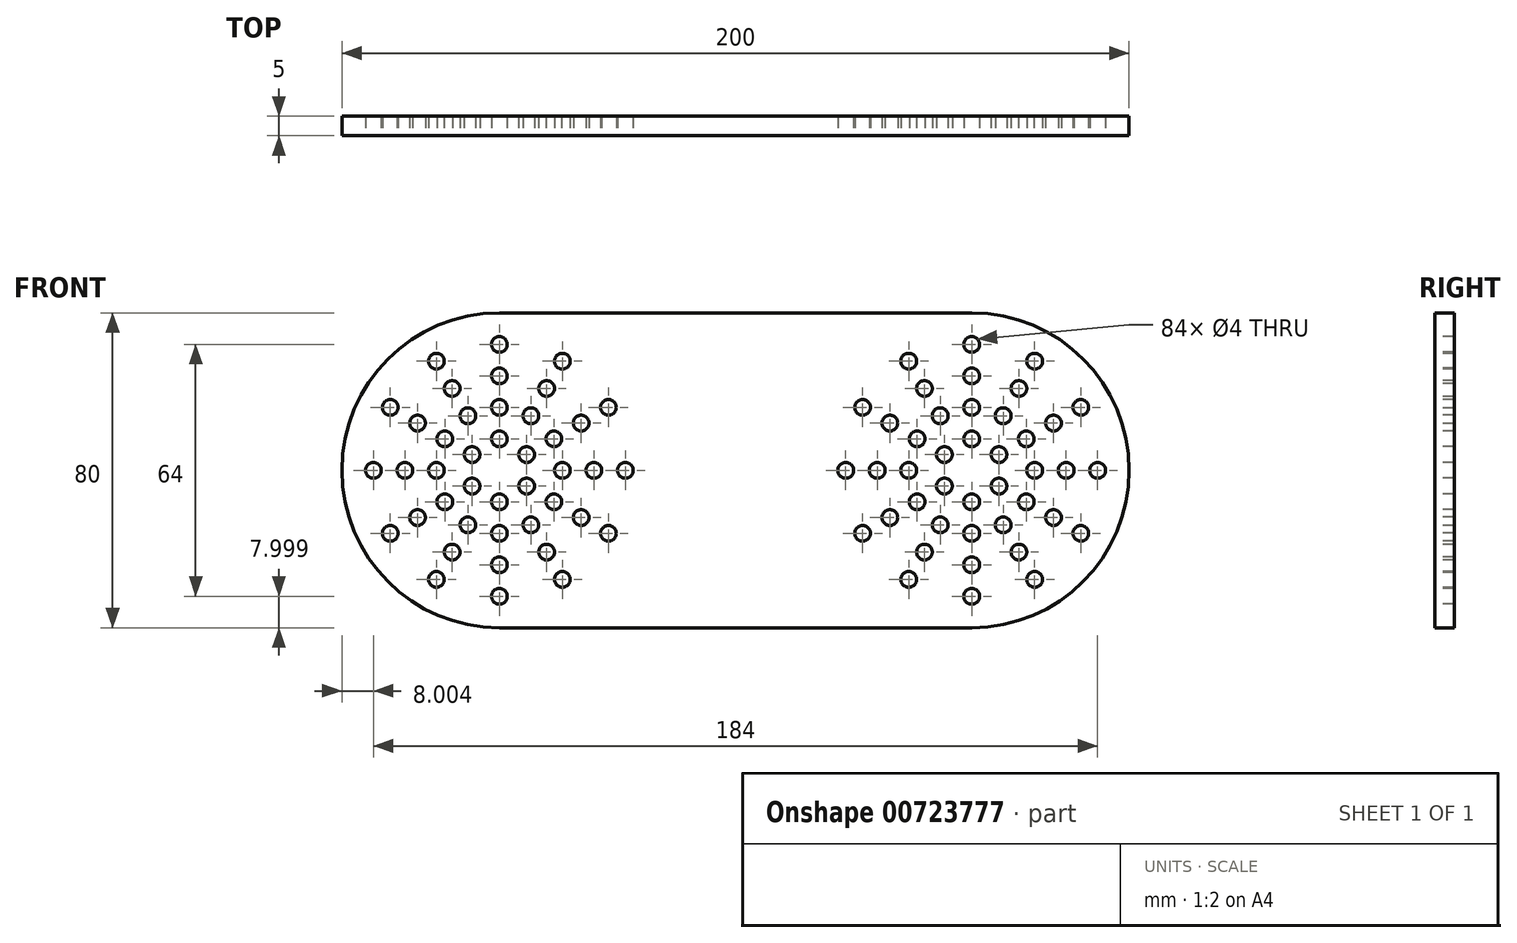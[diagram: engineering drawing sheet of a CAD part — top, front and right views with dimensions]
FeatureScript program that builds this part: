
annotation { "Feature Type Name" : "Feature", "Feature Type Description" : "" }
export const myFeature = defineFeature(function(context is Context, id is Id, definition is map)
    precondition{}
    {
        {
            var Q0;
            Q0=qCreatedBy(makeId("Front.planeOp"),FACE);
            var sketch = newSketch(context, id + "F0", { "sketchPlane" : qUnion([Q0])});
            skLineSegment(sketch, "E0.bottom", {"start": v(-63.67, 36.44) * mm, "end": v(56.33, 36.44) * mm});
            skLineSegment(sketch, "E0.top", {"start": v(-63.67, -43.56) * mm, "end": v(56.33, -43.56) * mm});
            skLineSegment(sketch, "E0.left", {"start": v(-103.67, -3.56) * mm, "end": v(-103.67, -3.56) * mm});
            skLineSegment(sketch, "E0.right", {"start": v(96.33, -3.56) * mm, "end": v(96.33, -3.56) * mm});
            skPoint(sketch, "E1.visualSharp", {"position": v(-103.67, 36.44) * mm});
            skArc(sketch, "E1.filletArc", {"start": v(-63.67, 36.44) * mm, "mid": v(-91.95, 24.72) * mm, "end": v(-103.67, -3.56) * mm});
            skPoint(sketch, "E2.visualSharp", {"position": v(-103.67, -43.56) * mm});
            skArc(sketch, "E2.filletArc", {"start": v(-103.67, -3.56) * mm, "mid": v(-91.95, -31.85) * mm, "end": v(-63.67, -43.56) * mm});
            skPoint(sketch, "E3.visualSharp", {"position": v(96.33, -43.56) * mm});
            skArc(sketch, "E3.filletArc", {"start": v(56.33, -43.56) * mm, "mid": v(84.62, -31.85) * mm, "end": v(96.33, -3.56) * mm});
            skPoint(sketch, "E4.visualSharp", {"position": v(96.33, 36.44) * mm});
            skArc(sketch, "E4.filletArc", {"start": v(96.33, -3.56) * mm, "mid": v(84.62, 24.72) * mm, "end": v(56.33, 36.44) * mm});
            skSolve(sketch);
        }
        {
            var Q0;
            Q0=makeQuery(id+"F0.imprint","IMPRINT",FACE,{"disambiguationData":[TD([[makeQuery(id+"F0.imprint","IMPRINT",EDGE,{"derivedFrom":sQuery(id+"F0.wireOp",EDGE,"E0.bottom")}),-1.0]])]});
            extrude(context, id + "F1", {"entities" : qUnion([Q0]), "depth" : 5 * mm});
        }
        {
            var Q0;
            Q0=makeQuery(id+"F1.opExtrude","CAP_FACE",FACE,{"disambiguationData":[OSD([sQuery(id+"F0.wireOp",EDGE,"E0.bottom"),sQuery(id+"F0.wireOp",EDGE,"E0.top"),sQuery(id+"F0.wireOp",EDGE,"E1.filletArc"),sQuery(id+"F0.wireOp",EDGE,"E2.filletArc"),sQuery(id+"F0.wireOp",EDGE,"E3.filletArc"),sQuery(id+"F0.wireOp",EDGE,"E4.filletArc")])],"isStart":false});
            var sketch = newSketch(context, id + "F2", { "sketchPlane" : qUnion([Q0])});
            skCircle(sketch, "E5", {"center": v(-63.67, -3.56) * mm, "radius": 33 * mm});
            skLineSegment(sketch, "E6", {"start": v(-3.67, 36.44) * mm, "end": v(-3.67, -43.56) * mm, "construction": true});
            skCircle(sketch, "E7.MirrorC", {"center": v(56.33, -3.56) * mm, "radius": 33 * mm});
            skSolve(sketch);
        }
        {
            var Q0;
            Q0=makeQuery(id+"F2.imprint","IMPRINT",FACE,{"disambiguationData":[TD([[makeQuery(id+"F2.imprint","IMPRINT",EDGE,{"derivedFrom":sQuery(id+"F2.wireOp",EDGE,"E5")}),1.0]])]});
            var sketch = newSketch(context, id + "F3", { "sketchPlane" : qUnion([Q0])});
            skCircle(sketch, "E8", {"center": v(-63.67, -3.56) * mm, "radius": 2 * mm, "construction": true});
            skCircle(sketch, "E9", {"center": v(-63.67, 28.44) * mm, "radius": 2 * mm});
            skCircle(sketch, "E10", {"center": v(-63.67, 20.44) * mm, "radius": 2 * mm});
            skCircle(sketch, "E11", {"center": v(-63.67, 12.44) * mm, "radius": 2 * mm});
            skCircle(sketch, "E12", {"center": v(-63.67, 4.44) * mm, "radius": 2 * mm});
            skCircle(sketch, "E13.1.0", {"center": v(-79.67, 24.15) * mm, "radius": 2 * mm});
            skCircle(sketch, "E13.1.1", {"center": v(-75.67, 17.22) * mm, "radius": 2 * mm});
            skCircle(sketch, "E13.1.2", {"center": v(-71.67, 10.3) * mm, "radius": 2 * mm});
            skCircle(sketch, "E13.2.0", {"center": v(-91.38, 12.44) * mm, "radius": 2 * mm});
            skCircle(sketch, "E13.2.1", {"center": v(-84.45, 8.44) * mm, "radius": 2 * mm});
            skCircle(sketch, "E13.2.2", {"center": v(-77.52, 4.44) * mm, "radius": 2 * mm});
            skCircle(sketch, "E13.2.3", {"center": v(-70.6, 0.44) * mm, "radius": 2 * mm});
            skCircle(sketch, "E13.3.0", {"center": v(-95.67, -3.56) * mm, "radius": 2 * mm});
            skCircle(sketch, "E13.3.1", {"center": v(-87.67, -3.56) * mm, "radius": 2 * mm});
            skCircle(sketch, "E13.3.2", {"center": v(-79.67, -3.56) * mm, "radius": 2 * mm});
            skCircle(sketch, "E13.4.0", {"center": v(-91.38, -19.56) * mm, "radius": 2 * mm});
            skCircle(sketch, "E13.4.1", {"center": v(-84.45, -15.56) * mm, "radius": 2 * mm});
            skCircle(sketch, "E13.4.2", {"center": v(-77.52, -11.56) * mm, "radius": 2 * mm});
            skCircle(sketch, "E13.4.3", {"center": v(-70.6, -7.56) * mm, "radius": 2 * mm});
            skCircle(sketch, "E13.5.0", {"center": v(-79.67, -31.27) * mm, "radius": 2 * mm});
            skCircle(sketch, "E13.5.1", {"center": v(-75.67, -24.35) * mm, "radius": 2 * mm});
            skCircle(sketch, "E13.5.2", {"center": v(-71.67, -17.42) * mm, "radius": 2 * mm});
            skCircle(sketch, "E13.6.0", {"center": v(-63.67, -35.56) * mm, "radius": 2 * mm});
            skCircle(sketch, "E13.6.1", {"center": v(-63.67, -27.56) * mm, "radius": 2 * mm});
            skCircle(sketch, "E13.6.2", {"center": v(-63.67, -19.56) * mm, "radius": 2 * mm});
            skCircle(sketch, "E13.6.3", {"center": v(-63.67, -11.56) * mm, "radius": 2 * mm});
            skCircle(sketch, "E13.7.0", {"center": v(-47.67, -31.27) * mm, "radius": 2 * mm});
            skCircle(sketch, "E13.7.1", {"center": v(-51.67, -24.35) * mm, "radius": 2 * mm});
            skCircle(sketch, "E13.7.2", {"center": v(-55.67, -17.42) * mm, "radius": 2 * mm});
            skCircle(sketch, "E13.8.0", {"center": v(-35.95, -19.56) * mm, "radius": 2 * mm});
            skCircle(sketch, "E13.8.1", {"center": v(-42.88, -15.56) * mm, "radius": 2 * mm});
            skCircle(sketch, "E13.8.2", {"center": v(-49.8, -11.56) * mm, "radius": 2 * mm});
            skCircle(sketch, "E13.8.3", {"center": v(-56.74, -7.56) * mm, "radius": 2 * mm});
            skCircle(sketch, "E13.9.0", {"center": v(-31.67, -3.56) * mm, "radius": 2 * mm});
            skCircle(sketch, "E13.9.1", {"center": v(-39.67, -3.56) * mm, "radius": 2 * mm});
            skCircle(sketch, "E13.9.2", {"center": v(-47.67, -3.56) * mm, "radius": 2 * mm});
            skCircle(sketch, "E13.10.0", {"center": v(-35.95, 12.44) * mm, "radius": 2 * mm});
            skCircle(sketch, "E13.10.1", {"center": v(-42.88, 8.44) * mm, "radius": 2 * mm});
            skCircle(sketch, "E13.10.2", {"center": v(-49.8, 4.44) * mm, "radius": 2 * mm});
            skCircle(sketch, "E13.10.3", {"center": v(-56.74, 0.44) * mm, "radius": 2 * mm});
            skCircle(sketch, "E13.11.0", {"center": v(-47.67, 24.15) * mm, "radius": 2 * mm});
            skCircle(sketch, "E13.11.1", {"center": v(-51.67, 17.22) * mm, "radius": 2 * mm});
            skCircle(sketch, "E13.11.2", {"center": v(-55.67, 10.3) * mm, "radius": 2 * mm});
            skCircle(sketch, "E14.MirrorC", {"center": v(56.33, -3.56) * mm, "radius": 2 * mm, "construction": true});
            skCircle(sketch, "E15.MirrorC", {"center": v(63.26, -7.56) * mm, "radius": 2 * mm});
            skCircle(sketch, "E16.MirrorC", {"center": v(49.4, -7.56) * mm, "radius": 2 * mm});
            skCircle(sketch, "E17.MirrorC", {"center": v(49.4, 0.44) * mm, "radius": 2 * mm});
            skCircle(sketch, "E18.MirrorC", {"center": v(56.33, 20.44) * mm, "radius": 2 * mm});
            skCircle(sketch, "E19.MirrorC", {"center": v(56.33, 4.44) * mm, "radius": 2 * mm});
            skCircle(sketch, "E20.MirrorC", {"center": v(77.12, -15.56) * mm, "radius": 2 * mm});
            skCircle(sketch, "E21.MirrorC", {"center": v(63.26, 0.44) * mm, "radius": 2 * mm});
            skCircle(sketch, "E22.MirrorC", {"center": v(56.33, -27.56) * mm, "radius": 2 * mm});
            skCircle(sketch, "E23.MirrorC", {"center": v(40.33, 24.15) * mm, "radius": 2 * mm});
            skCircle(sketch, "E24.MirrorC", {"center": v(42.48, 4.44) * mm, "radius": 2 * mm});
            skCircle(sketch, "E25.MirrorC", {"center": v(70.2, -11.56) * mm, "radius": 2 * mm});
            skCircle(sketch, "E26.MirrorC", {"center": v(56.33, -11.56) * mm, "radius": 2 * mm});
            skCircle(sketch, "E27.MirrorC", {"center": v(84.05, -19.56) * mm, "radius": 2 * mm});
            skCircle(sketch, "E28.MirrorC", {"center": v(64.33, -17.42) * mm, "radius": 2 * mm});
            skCircle(sketch, "E29.MirrorC", {"center": v(40.33, -3.56) * mm, "radius": 2 * mm});
            skCircle(sketch, "E30.MirrorC", {"center": v(35.55, 8.44) * mm, "radius": 2 * mm});
            skCircle(sketch, "E31.MirrorC", {"center": v(44.33, 17.22) * mm, "radius": 2 * mm});
            skCircle(sketch, "E32.MirrorC", {"center": v(24.33, -3.56) * mm, "radius": 2 * mm});
            skCircle(sketch, "E33.MirrorC", {"center": v(44.33, -24.35) * mm, "radius": 2 * mm});
            skCircle(sketch, "E34.MirrorC", {"center": v(40.33, -31.27) * mm, "radius": 2 * mm});
            skCircle(sketch, "E35.MirrorC", {"center": v(72.33, -31.27) * mm, "radius": 2 * mm});
            skCircle(sketch, "E36.MirrorC", {"center": v(56.33, -19.56) * mm, "radius": 2 * mm});
            skCircle(sketch, "E37.MirrorC", {"center": v(42.48, -11.56) * mm, "radius": 2 * mm});
            skCircle(sketch, "E38.MirrorC", {"center": v(28.62, -19.56) * mm, "radius": 2 * mm});
            skCircle(sketch, "E39.MirrorC", {"center": v(88.33, -3.56) * mm, "radius": 2 * mm});
            skCircle(sketch, "E40.MirrorC", {"center": v(80.33, -3.56) * mm, "radius": 2 * mm});
            skCircle(sketch, "E41.MirrorC", {"center": v(72.33, -3.56) * mm, "radius": 2 * mm});
            skCircle(sketch, "E42.MirrorC", {"center": v(28.62, 12.44) * mm, "radius": 2 * mm});
            skCircle(sketch, "E43.MirrorC", {"center": v(56.33, -35.56) * mm, "radius": 2 * mm});
            skCircle(sketch, "E44.MirrorC", {"center": v(56.33, 28.44) * mm, "radius": 2 * mm});
            skCircle(sketch, "E45.MirrorC", {"center": v(56.33, 12.44) * mm, "radius": 2 * mm});
            skCircle(sketch, "E46.MirrorC", {"center": v(48.33, 10.3) * mm, "radius": 2 * mm});
            skCircle(sketch, "E47.MirrorC", {"center": v(48.33, -17.42) * mm, "radius": 2 * mm});
            skCircle(sketch, "E48.MirrorC", {"center": v(32.33, -3.56) * mm, "radius": 2 * mm});
            skCircle(sketch, "E49.MirrorC", {"center": v(68.33, -24.35) * mm, "radius": 2 * mm});
            skCircle(sketch, "E50.MirrorC", {"center": v(72.33, 24.15) * mm, "radius": 2 * mm});
            skCircle(sketch, "E51.MirrorC", {"center": v(68.33, 17.22) * mm, "radius": 2 * mm});
            skCircle(sketch, "E52.MirrorC", {"center": v(35.55, -15.56) * mm, "radius": 2 * mm});
            skCircle(sketch, "E53.MirrorC", {"center": v(64.33, 10.3) * mm, "radius": 2 * mm});
            skCircle(sketch, "E54.MirrorC", {"center": v(84.05, 12.44) * mm, "radius": 2 * mm});
            skCircle(sketch, "E55.MirrorC", {"center": v(77.12, 8.44) * mm, "radius": 2 * mm});
            skCircle(sketch, "E56.MirrorC", {"center": v(70.2, 4.44) * mm, "radius": 2 * mm});
            skSolve(sketch);
        }
        {
            var Q0;
            Q0=qSketchRegion(id+"F3",true);
            extrude(context, id + "F4", {"entities" : qUnion([Q0]), "operationType" : NewBodyOperationType.REMOVE, "endBound" : BoundingType.UP_TO_NEXT, "oppositeDirection" : true, "depth" : 25 * mm});
        }
    });
